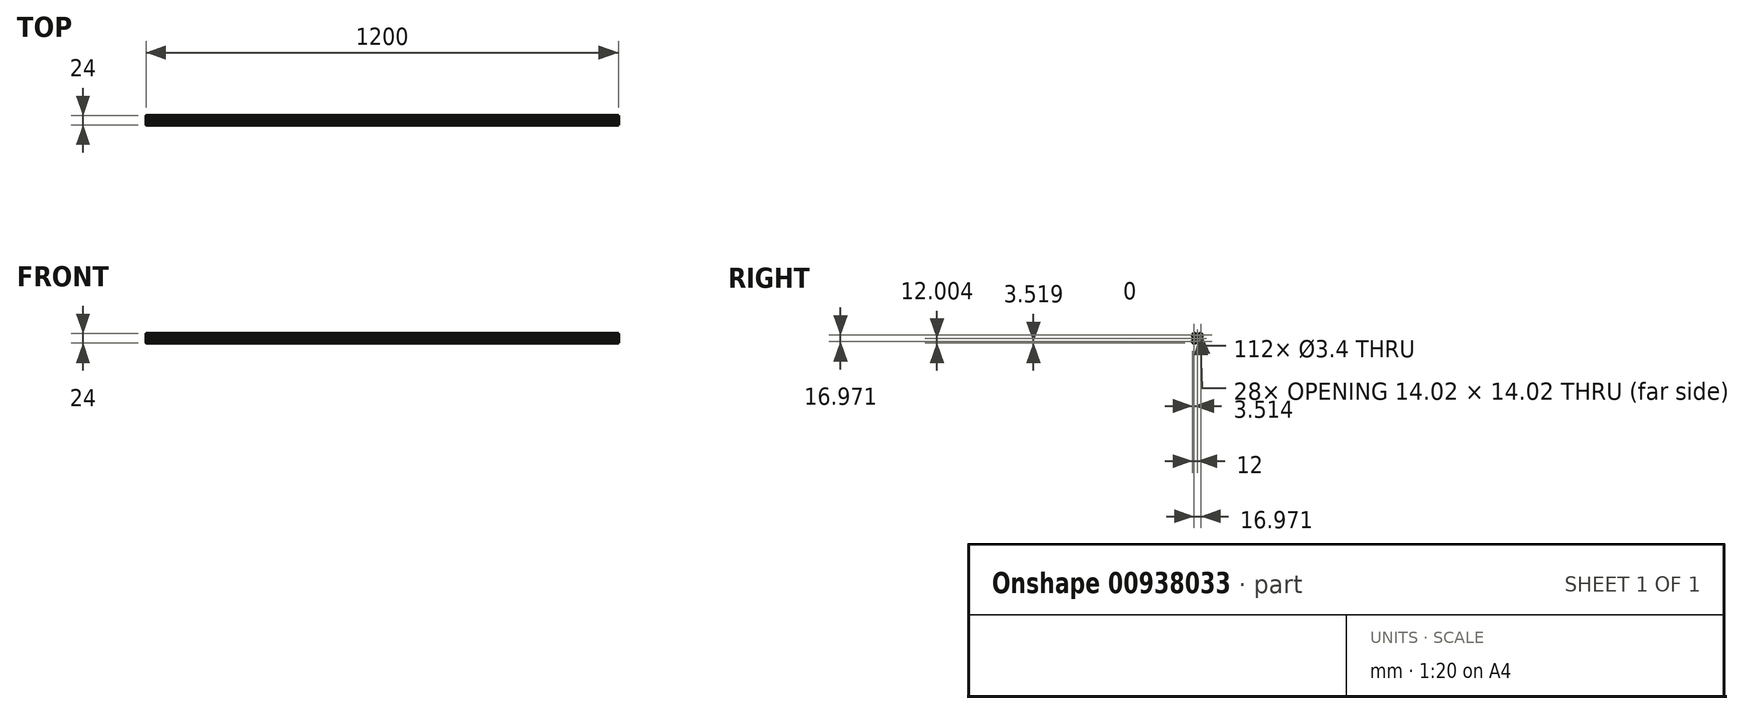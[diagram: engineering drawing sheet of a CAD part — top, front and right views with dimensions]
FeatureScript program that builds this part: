
annotation { "Feature Type Name" : "Feature", "Feature Type Description" : "" }
export const myFeature = defineFeature(function(context is Context, id is Id, definition is map)
    precondition{}
    {
        {
            var Q0;
            Q0=qCreatedBy(makeId("Right.planeOp"),FACE);
            var sketch = newSketch(context, id + "F0", { "sketchPlane" : qUnion([Q0]) });
            skLineSegment(sketch, "E0.0.0", {"start": v(-5.44, -8.54) * mm, "end": v(5.56, -8.54) * mm});
            skLineSegment(sketch, "E0.0.1", {"start": v(5.56, -8.54) * mm, "end": v(5.56, -10.04) * mm});
            skLineSegment(sketch, "E0.0.2", {"start": v(5.56, -10.04) * mm, "end": v(4.06, -10.04) * mm});
            skLineSegment(sketch, "E0.0.3", {"start": v(4.06, -10.04) * mm, "end": v(4.06, -11.04) * mm});
            skLineSegment(sketch, "E0.0.4", {"start": v(4.06, -11.04) * mm, "end": v(5.06, -12.04) * mm});
            skLineSegment(sketch, "E0.0.5", {"start": v(5.06, -12.04) * mm, "end": v(8.04, -12.04) * mm});
            skLineSegment(sketch, "E0.0.6", {"start": v(8.04, -12.04) * mm, "end": v(8.54, -11.54) * mm});
            skLineSegment(sketch, "E0.0.7", {"start": v(8.54, -11.54) * mm, "end": v(9.04, -12.04) * mm});
            skLineSegment(sketch, "E0.0.8", {"start": v(9.04, -12.04) * mm, "end": v(10.57, -12.04) * mm});
            skArc(sketch, "E0.0.9", {"start": v(10.57, -12.04) * mm, "mid": v(11.34, -11.31) * mm, "end": v(12.06, -10.54) * mm});
            skLineSegment(sketch, "E0.0.10", {"start": v(12.06, -10.54) * mm, "end": v(12.06, -9.02) * mm});
            skLineSegment(sketch, "E0.0.11", {"start": v(12.06, -9.02) * mm, "end": v(11.56, -8.52) * mm});
            skLineSegment(sketch, "E0.0.12", {"start": v(11.56, -8.52) * mm, "end": v(12.06, -8.02) * mm});
            skLineSegment(sketch, "E0.0.13", {"start": v(12.06, -8.02) * mm, "end": v(12.06, -5.04) * mm});
            skLineSegment(sketch, "E0.0.14", {"start": v(12.06, -5.04) * mm, "end": v(11.06, -4.04) * mm});
            skLineSegment(sketch, "E0.0.15", {"start": v(11.06, -4.04) * mm, "end": v(10.06, -4.04) * mm});
            skLineSegment(sketch, "E0.0.16", {"start": v(10.06, -4.04) * mm, "end": v(10.06, -5.54) * mm});
            skLineSegment(sketch, "E0.0.17", {"start": v(10.06, -5.54) * mm, "end": v(8.56, -5.54) * mm});
            skLineSegment(sketch, "E0.0.18", {"start": v(8.56, -5.54) * mm, "end": v(8.56, 5.46) * mm});
            skLineSegment(sketch, "E0.0.19", {"start": v(8.56, 5.46) * mm, "end": v(10.06, 5.46) * mm});
            skLineSegment(sketch, "E0.0.20", {"start": v(10.06, 5.46) * mm, "end": v(10.06, 3.96) * mm});
            skLineSegment(sketch, "E0.0.21", {"start": v(10.06, 3.96) * mm, "end": v(11.06, 3.96) * mm});
            skLineSegment(sketch, "E0.0.22", {"start": v(11.06, 3.96) * mm, "end": v(12.06, 4.96) * mm});
            skLineSegment(sketch, "E0.0.23", {"start": v(12.06, 4.96) * mm, "end": v(12.06, 7.95) * mm});
            skLineSegment(sketch, "E0.0.24", {"start": v(12.06, 7.95) * mm, "end": v(11.56, 8.45) * mm});
            skLineSegment(sketch, "E0.0.25", {"start": v(11.56, 8.45) * mm, "end": v(12.06, 8.95) * mm});
            skLineSegment(sketch, "E0.0.26", {"start": v(12.06, 8.95) * mm, "end": v(12.06, 10.47) * mm});
            skArc(sketch, "E0.0.27", {"start": v(12.06, 10.47) * mm, "mid": v(11.34, 11.24) * mm, "end": v(10.57, 11.96) * mm});
            skLineSegment(sketch, "E0.0.28", {"start": v(10.57, 11.96) * mm, "end": v(9.04, 11.96) * mm});
            skLineSegment(sketch, "E0.0.29", {"start": v(9.04, 11.96) * mm, "end": v(8.54, 11.46) * mm});
            skLineSegment(sketch, "E0.0.30", {"start": v(8.54, 11.46) * mm, "end": v(8.04, 11.96) * mm});
            skLineSegment(sketch, "E0.0.31", {"start": v(8.04, 11.96) * mm, "end": v(5.06, 11.96) * mm});
            skLineSegment(sketch, "E0.0.32", {"start": v(5.06, 11.96) * mm, "end": v(4.06, 10.96) * mm});
            skLineSegment(sketch, "E0.0.33", {"start": v(4.06, 10.96) * mm, "end": v(4.06, 9.96) * mm});
            skLineSegment(sketch, "E0.0.34", {"start": v(4.06, 9.96) * mm, "end": v(5.56, 9.96) * mm});
            skLineSegment(sketch, "E0.0.35", {"start": v(5.56, 9.96) * mm, "end": v(5.56, 8.46) * mm});
            skLineSegment(sketch, "E0.0.36", {"start": v(5.56, 8.46) * mm, "end": v(-5.44, 8.46) * mm});
            skLineSegment(sketch, "E0.0.37", {"start": v(-5.44, 8.46) * mm, "end": v(-5.44, 9.96) * mm});
            skLineSegment(sketch, "E0.0.38", {"start": v(-5.44, 9.96) * mm, "end": v(-3.94, 9.96) * mm});
            skLineSegment(sketch, "E0.0.39", {"start": v(-3.94, 9.96) * mm, "end": v(-3.94, 10.96) * mm});
            skLineSegment(sketch, "E0.0.40", {"start": v(-3.94, 10.96) * mm, "end": v(-4.94, 11.96) * mm});
            skLineSegment(sketch, "E0.0.41", {"start": v(-4.94, 11.96) * mm, "end": v(-7.93, 11.96) * mm});
            skLineSegment(sketch, "E0.0.42", {"start": v(-7.93, 11.96) * mm, "end": v(-8.43, 11.46) * mm});
            skLineSegment(sketch, "E0.0.43", {"start": v(-8.43, 11.46) * mm, "end": v(-8.93, 11.96) * mm});
            skLineSegment(sketch, "E0.0.44", {"start": v(-8.93, 11.96) * mm, "end": v(-10.45, 11.96) * mm});
            skArc(sketch, "E0.0.45", {"start": v(-10.45, 11.96) * mm, "mid": v(-11.22, 11.24) * mm, "end": v(-11.94, 10.47) * mm});
            skLineSegment(sketch, "E0.0.46", {"start": v(-11.94, 10.47) * mm, "end": v(-11.94, 8.95) * mm});
            skLineSegment(sketch, "E0.0.47", {"start": v(-11.94, 8.95) * mm, "end": v(-11.44, 8.45) * mm});
            skLineSegment(sketch, "E0.0.48", {"start": v(-11.44, 8.45) * mm, "end": v(-11.94, 7.95) * mm});
            skLineSegment(sketch, "E0.0.49", {"start": v(-11.94, 7.95) * mm, "end": v(-11.94, 4.96) * mm});
            skLineSegment(sketch, "E0.0.50", {"start": v(-11.94, 4.96) * mm, "end": v(-10.94, 3.96) * mm});
            skLineSegment(sketch, "E0.0.51", {"start": v(-10.94, 3.96) * mm, "end": v(-9.94, 3.96) * mm});
            skLineSegment(sketch, "E0.0.52", {"start": v(-9.94, 3.96) * mm, "end": v(-9.94, 5.46) * mm});
            skLineSegment(sketch, "E0.0.53", {"start": v(-9.94, 5.46) * mm, "end": v(-8.44, 5.46) * mm});
            skLineSegment(sketch, "E0.0.54", {"start": v(-8.44, 5.46) * mm, "end": v(-8.44, -5.54) * mm});
            skLineSegment(sketch, "E0.0.55", {"start": v(-8.44, -5.54) * mm, "end": v(-9.94, -5.54) * mm});
            skLineSegment(sketch, "E0.0.56", {"start": v(-9.94, -5.54) * mm, "end": v(-9.94, -4.04) * mm});
            skLineSegment(sketch, "E0.0.57", {"start": v(-9.94, -4.04) * mm, "end": v(-10.94, -4.04) * mm});
            skLineSegment(sketch, "E0.0.58", {"start": v(-10.94, -4.04) * mm, "end": v(-11.94, -5.04) * mm});
            skLineSegment(sketch, "E0.0.59", {"start": v(-11.94, -5.04) * mm, "end": v(-11.94, -8.02) * mm});
            skLineSegment(sketch, "E0.0.60", {"start": v(-11.94, -8.02) * mm, "end": v(-11.44, -8.52) * mm});
            skLineSegment(sketch, "E0.0.61", {"start": v(-11.44, -8.52) * mm, "end": v(-11.94, -9.02) * mm});
            skLineSegment(sketch, "E0.0.62", {"start": v(-11.94, -9.02) * mm, "end": v(-11.94, -10.54) * mm});
            skArc(sketch, "E0.0.63", {"start": v(-11.94, -10.54) * mm, "mid": v(-11.22, -11.31) * mm, "end": v(-10.45, -12.04) * mm});
            skLineSegment(sketch, "E0.0.64", {"start": v(-10.45, -12.04) * mm, "end": v(-8.93, -12.04) * mm});
            skLineSegment(sketch, "E0.0.65", {"start": v(-8.93, -12.04) * mm, "end": v(-8.43, -11.54) * mm});
            skLineSegment(sketch, "E0.0.66", {"start": v(-8.43, -11.54) * mm, "end": v(-7.93, -12.04) * mm});
            skLineSegment(sketch, "E0.0.67", {"start": v(-7.93, -12.04) * mm, "end": v(-4.94, -12.04) * mm});
            skLineSegment(sketch, "E0.0.68", {"start": v(-4.94, -12.04) * mm, "end": v(-3.94, -11.04) * mm});
            skLineSegment(sketch, "E0.0.69", {"start": v(-3.94, -11.04) * mm, "end": v(-3.94, -10.04) * mm});
            skLineSegment(sketch, "E0.0.70", {"start": v(-3.94, -10.04) * mm, "end": v(-5.44, -10.04) * mm});
            skLineSegment(sketch, "E0.0.71", {"start": v(-5.44, -10.04) * mm, "end": v(-5.44, -8.54) * mm});
            skCircle(sketch, "E1.0", {"center": v(8.54, -8.52) * mm, "radius": 1.7 * mm});
            skCircle(sketch, "E2.0", {"center": v(-8.43, -8.52) * mm, "radius": 1.7 * mm});
            skArc(sketch, "E3.0", {"start": v(3.57, -6.1) * mm, "mid": v(0.06, -7.05) * mm, "end": v(-3.45, -6.1) * mm});
            skLineSegment(sketch, "E4.0", {"start": v(-3.7, -6.04) * mm, "end": v(-5.44, -6.04) * mm});
            skArc(sketch, "E5.0", {"start": v(-3.45, -6.1) * mm, "mid": v(-3.57, -6.05) * mm, "end": v(-3.7, -6.04) * mm});
            skArc(sketch, "E6.0", {"start": v(-5.44, -6.04) * mm, "mid": v(-5.8, -5.89) * mm, "end": v(-5.94, -5.54) * mm});
            skLineSegment(sketch, "E7.0", {"start": v(-5.94, -3.8) * mm, "end": v(-5.94, -5.54) * mm});
            skArc(sketch, "E8.0", {"start": v(-6, -3.55) * mm, "mid": v(-6.95, -0.04) * mm, "end": v(-6, 3.48) * mm});
            skArc(sketch, "E9.0", {"start": v(-5.94, -3.8) * mm, "mid": v(-5.96, -3.67) * mm, "end": v(-6, -3.55) * mm});
            skLineSegment(sketch, "E10.0", {"start": v(-5.94, 5.46) * mm, "end": v(-5.94, 3.73) * mm});
            skPoint(sketch, "E11.0", {"position": v(-5.96, 3.6) * mm});
            skArc(sketch, "E12.0", {"start": v(-5.94, 5.46) * mm, "mid": v(-5.8, 5.82) * mm, "end": v(-5.44, 5.96) * mm});
            skLineSegment(sketch, "E13.0", {"start": v(-3.7, 5.96) * mm, "end": v(-5.44, 5.96) * mm});
            skArc(sketch, "E14.0", {"start": v(-3.45, 6.03) * mm, "mid": v(0.06, 6.97) * mm, "end": v(3.57, 6.03) * mm});
            skArc(sketch, "E15.0", {"start": v(-3.7, 5.96) * mm, "mid": v(-3.57, 5.98) * mm, "end": v(-3.45, 6.03) * mm});
            skLineSegment(sketch, "E16.0", {"start": v(5.56, 5.96) * mm, "end": v(3.82, 5.96) * mm});
            skArc(sketch, "E17.0", {"start": v(3.57, 6.03) * mm, "mid": v(3.7, 5.98) * mm, "end": v(3.82, 5.96) * mm});
            skArc(sketch, "E18.0", {"start": v(5.56, 5.96) * mm, "mid": v(5.91, 5.82) * mm, "end": v(6.06, 5.46) * mm});
            skLineSegment(sketch, "E19.0", {"start": v(6.06, 5.46) * mm, "end": v(6.06, 3.73) * mm});
            skArc(sketch, "E20.0", {"start": v(6.13, 3.48) * mm, "mid": v(7.07, -0.04) * mm, "end": v(6.13, -3.55) * mm});
            skArc(sketch, "E21.0", {"start": v(6.06, 3.73) * mm, "mid": v(6.08, 3.6) * mm, "end": v(6.13, 3.48) * mm});
            skCircle(sketch, "E22.0", {"center": v(-8.43, 8.45) * mm, "radius": 1.7 * mm});
            skCircle(sketch, "E23.0", {"center": v(8.54, 8.45) * mm, "radius": 1.7 * mm});
            skLineSegment(sketch, "E24.0", {"start": v(5.56, -6.04) * mm, "end": v(3.82, -6.04) * mm});
            skArc(sketch, "E25.0", {"start": v(6.06, -5.54) * mm, "mid": v(5.91, -5.89) * mm, "end": v(5.56, -6.04) * mm});
            skLineSegment(sketch, "E26.0", {"start": v(6.06, -3.8) * mm, "end": v(6.06, -5.54) * mm});
            skArc(sketch, "E27.0", {"start": v(3.82, -6.04) * mm, "mid": v(3.7, -6.05) * mm, "end": v(3.57, -6.1) * mm});
            skArc(sketch, "E28.0", {"start": v(6.13, -3.55) * mm, "mid": v(6.08, -3.67) * mm, "end": v(6.06, -3.8) * mm});
            skArc(sketch, "E29.0", {"start": v(-6, 3.48) * mm, "mid": v(-5.96, 3.6) * mm, "end": v(-5.94, 3.73) * mm});
            skSolve(sketch);
        }
        {
            var Q0;
            Q0=qSketchRegion(id+"F0",true);
            extrude(context, id + "F1", {"entities" : qUnion([Q0]), "depth" : 48 * mm, "offsetDistance" : 25 * mm});
        }
        {
            var Q0;
            Q0=qSketchRegion(id+"F0",true);
            extrude(context, id + "F2", {"entities" : qUnion([Q0]), "depth" : 72 * mm, "offsetDistance" : 25 * mm});
        }
        {
            var Q0;
            Q0=qSketchRegion(id+"F0",true);
            extrude(context, id + "F3", {"entities" : qUnion([Q0]), "depth" : 96 * mm, "offsetDistance" : 25 * mm});
        }
        {
            var Q0;
            Q0=qSketchRegion(id+"F0",true);
            extrude(context, id + "F4", {"entities" : qUnion([Q0]), "depth" : 120 * mm, "offsetDistance" : 25 * mm});
        }
        {
            var Q0;
            Q0=qSketchRegion(id+"F0",true);
            extrude(context, id + "F5", {"entities" : qUnion([Q0]), "depth" : 144 * mm, "offsetDistance" : 25 * mm});
        }
        {
            var Q0;
            Q0=qSketchRegion(id+"F0",true);
            extrude(context, id + "F6", {"entities" : qUnion([Q0]), "depth" : 192 * mm, "offsetDistance" : 25 * mm});
        }
        {
            var Q0;
            Q0=qSketchRegion(id+"F0",true);
            extrude(context, id + "F7", {"entities" : qUnion([Q0]), "depth" : 288 * mm, "offsetDistance" : 25 * mm});
        }
        {
            var Q0;
            Q0=qSketchRegion(id+"F0",true);
            extrude(context, id + "F8", {"entities" : qUnion([Q0]), "depth" : 336 * mm, "offsetDistance" : 25 * mm});
        }
        {
            var Q0;
            Q0=qSketchRegion(id+"F0",true);
            extrude(context, id + "F9", {"entities" : qUnion([Q0]), "depth" : 384 * mm, "offsetDistance" : 25 * mm});
        }
        {
            var Q0;
            Q0=qSketchRegion(id+"F0",true);
            extrude(context, id + "F10", {"entities" : qUnion([Q0]), "depth" : 432 * mm, "offsetDistance" : 25 * mm});
        }
        {
            var Q0;
            Q0=qSketchRegion(id+"F0",true);
            extrude(context, id + "F11", {"entities" : qUnion([Q0]), "depth" : 528 * mm, "offsetDistance" : 25 * mm});
        }
        {
            var Q0;
            Q0=qSketchRegion(id+"F0",true);
            extrude(context, id + "F12", {"entities" : qUnion([Q0]), "depth" : 624 * mm, "offsetDistance" : 25 * mm});
        }
        {
            var Q0;
            Q0=qSketchRegion(id+"F0",true);
            extrude(context, id + "F13", {"entities" : qUnion([Q0]), "depth" : 912 * mm, "offsetDistance" : 25 * mm});
        }
        {
            var Q0;
            Q0=qSketchRegion(id+"F0",true);
            extrude(context, id + "F14", {"entities" : qUnion([Q0]), "depth" : 1200 * mm, "offsetDistance" : 25 * mm});
        }
    });
